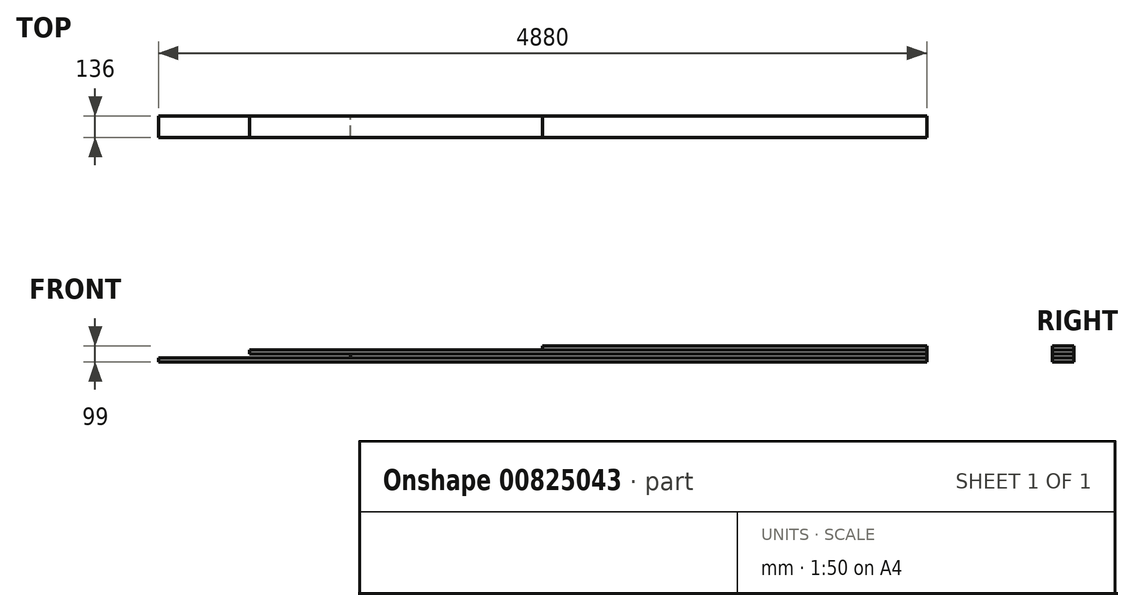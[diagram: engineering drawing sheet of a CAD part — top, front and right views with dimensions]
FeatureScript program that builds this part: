
annotation { "Feature Type Name" : "Feature", "Feature Type Description" : "" }
export const myFeature = defineFeature(function(context is Context, id is Id, definition is map)
    precondition{}
    {
        {
            var Q0;
            Q0=qCreatedBy(makeId("Right.planeOp"),FACE);
            var sketch = newSketch(context, id + "F0", { "sketchPlane" : qUnion([Q0])});
            skLineSegment(sketch, "E0.bottom", {"start": v(0, 0) * mm, "end": v(136, 0) * mm});
            skLineSegment(sketch, "E0.top", {"start": v(0, 24) * mm, "end": v(136, 24) * mm});
            skLineSegment(sketch, "E0.left", {"start": v(0, 0) * mm, "end": v(0, 24) * mm});
            skLineSegment(sketch, "E0.right", {"start": v(136, 0) * mm, "end": v(136, 24) * mm});
            skLineSegment(sketch, "E1.0.1.0", {"start": v(136, 25) * mm, "end": v(136, 49) * mm});
            skLineSegment(sketch, "E1.0.1.1", {"start": v(0, 49) * mm, "end": v(136, 49) * mm});
            skLineSegment(sketch, "E1.0.1.2", {"start": v(0, 25) * mm, "end": v(0, 49) * mm});
            skLineSegment(sketch, "E1.0.1.3", {"start": v(0, 25) * mm, "end": v(136, 25) * mm});
            skLineSegment(sketch, "E1.0.2.0", {"start": v(136, 50) * mm, "end": v(136, 74) * mm});
            skLineSegment(sketch, "E1.0.2.1", {"start": v(0, 74) * mm, "end": v(136, 74) * mm});
            skLineSegment(sketch, "E1.0.2.2", {"start": v(0, 50) * mm, "end": v(0, 74) * mm});
            skLineSegment(sketch, "E1.0.2.3", {"start": v(0, 50) * mm, "end": v(136, 50) * mm});
            skLineSegment(sketch, "E1.direction1", {"start": v(25, 24) * mm, "end": v(136, 24) * mm, "construction": true});
            skLineSegment(sketch, "E1.direction2", {"start": v(136, 24) * mm, "end": v(136, 49) * mm, "construction": true});
            skLineSegment(sketch, "E2.0.0.3", {"start": v(136, 75) * mm, "end": v(136, 99) * mm});
            skLineSegment(sketch, "E2.3.0.3", {"start": v(0, 99) * mm, "end": v(136, 99) * mm});
            skLineSegment(sketch, "E2.6.0.3", {"start": v(0, 75) * mm, "end": v(0, 99) * mm});
            skLineSegment(sketch, "E2.9.0.3", {"start": v(0, 75) * mm, "end": v(136, 75) * mm});
            skLineSegment(sketch, "E2.0.0.4", {"start": v(136, 100) * mm, "end": v(136, 124) * mm});
            skLineSegment(sketch, "E2.3.0.4", {"start": v(0, 124) * mm, "end": v(136, 124) * mm});
            skLineSegment(sketch, "E2.6.0.4", {"start": v(0, 100) * mm, "end": v(0, 124) * mm});
            skLineSegment(sketch, "E2.9.0.4", {"start": v(0, 100) * mm, "end": v(136, 100) * mm});
            skLineSegment(sketch, "E2.0.0.5", {"start": v(136, 125) * mm, "end": v(136, 149) * mm});
            skLineSegment(sketch, "E2.3.0.5", {"start": v(0, 149) * mm, "end": v(136, 149) * mm});
            skLineSegment(sketch, "E2.6.0.5", {"start": v(0, 125) * mm, "end": v(0, 149) * mm});
            skLineSegment(sketch, "E2.9.0.5", {"start": v(0, 125) * mm, "end": v(136, 125) * mm});
            skLineSegment(sketch, "E2.0.0.6", {"start": v(136, 150) * mm, "end": v(136, 174) * mm});
            skLineSegment(sketch, "E2.3.0.6", {"start": v(0, 174) * mm, "end": v(136, 174) * mm});
            skLineSegment(sketch, "E2.6.0.6", {"start": v(0, 150) * mm, "end": v(0, 174) * mm});
            skLineSegment(sketch, "E2.9.0.6", {"start": v(0, 150) * mm, "end": v(136, 150) * mm});
            skLineSegment(sketch, "E2.0.0.7", {"start": v(136, 175) * mm, "end": v(136, 199) * mm});
            skLineSegment(sketch, "E2.3.0.7", {"start": v(0, 199) * mm, "end": v(136, 199) * mm});
            skLineSegment(sketch, "E2.6.0.7", {"start": v(0, 175) * mm, "end": v(0, 199) * mm});
            skLineSegment(sketch, "E2.9.0.7", {"start": v(0, 175) * mm, "end": v(136, 175) * mm});
            skLineSegment(sketch, "E2.0.0.8", {"start": v(136, 200) * mm, "end": v(136, 224) * mm});
            skLineSegment(sketch, "E2.3.0.8", {"start": v(0, 224) * mm, "end": v(136, 224) * mm});
            skLineSegment(sketch, "E2.6.0.8", {"start": v(0, 200) * mm, "end": v(0, 224) * mm});
            skLineSegment(sketch, "E2.9.0.8", {"start": v(0, 200) * mm, "end": v(136, 200) * mm});
            skLineSegment(sketch, "E2.0.0.9", {"start": v(136, 225) * mm, "end": v(136, 249) * mm});
            skLineSegment(sketch, "E2.3.0.9", {"start": v(0, 249) * mm, "end": v(136, 249) * mm});
            skLineSegment(sketch, "E2.6.0.9", {"start": v(0, 225) * mm, "end": v(0, 249) * mm});
            skLineSegment(sketch, "E2.9.0.9", {"start": v(0, 225) * mm, "end": v(136, 225) * mm});
            skSolve(sketch);
        }
        {
            var Q0;
            Q0=makeQuery(id+"F0.imprint","IMPRINT",FACE,{"disambiguationData":[TD([[makeQuery(id+"F0.imprint","IMPRINT",EDGE,{"derivedFrom":sQuery(id+"F0.wireOp",EDGE,"E0.bottom")}),1.0]])]});
            extrude(context, id + "F1", {"entities" : qUnion([Q0]), "oppositeDirection" : true, "depth" : 4880 * mm, "offsetDistance" : 25 * mm});
        }
        {
            var Q0;
            Q0=makeQuery(id+"F0.imprint","IMPRINT",FACE,{"disambiguationData":[TD([[makeQuery(id+"F0.imprint","IMPRINT",EDGE,{"derivedFrom":sQuery(id+"F0.wireOp",EDGE,"E1.0.1.0")}),1.0]])]});
            extrude(context, id + "F2", {"entities" : qUnion([Q0]), "oppositeDirection" : true, "depth" : 3660 * mm, "offsetDistance" : 25 * mm});
        }
        {
            var Q0;
            Q0=makeQuery(id+"F0.imprint","IMPRINT",FACE,{"disambiguationData":[TD([[makeQuery(id+"F0.imprint","IMPRINT",EDGE,{"derivedFrom":sQuery(id+"F0.wireOp",EDGE,"E1.0.2.0")}),1.0]])]});
            extrude(context, id + "F3", {"entities" : qUnion([Q0]), "oppositeDirection" : true, "depth" : 4300 * mm, "offsetDistance" : 25 * mm});
        }
        {
            var Q0;
            Q0=makeQuery(id+"F0.imprint","IMPRINT",FACE,{"disambiguationData":[TD([[makeQuery(id+"F0.imprint","IMPRINT",EDGE,{"derivedFrom":sQuery(id+"F0.wireOp",EDGE,"E2.0.0.3")}),1.0]])]});
            extrude(context, id + "F4", {"entities" : qUnion([Q0]), "oppositeDirection" : true, "depth" : 2440 * mm, "offsetDistance" : 25 * mm});
        }
    });
